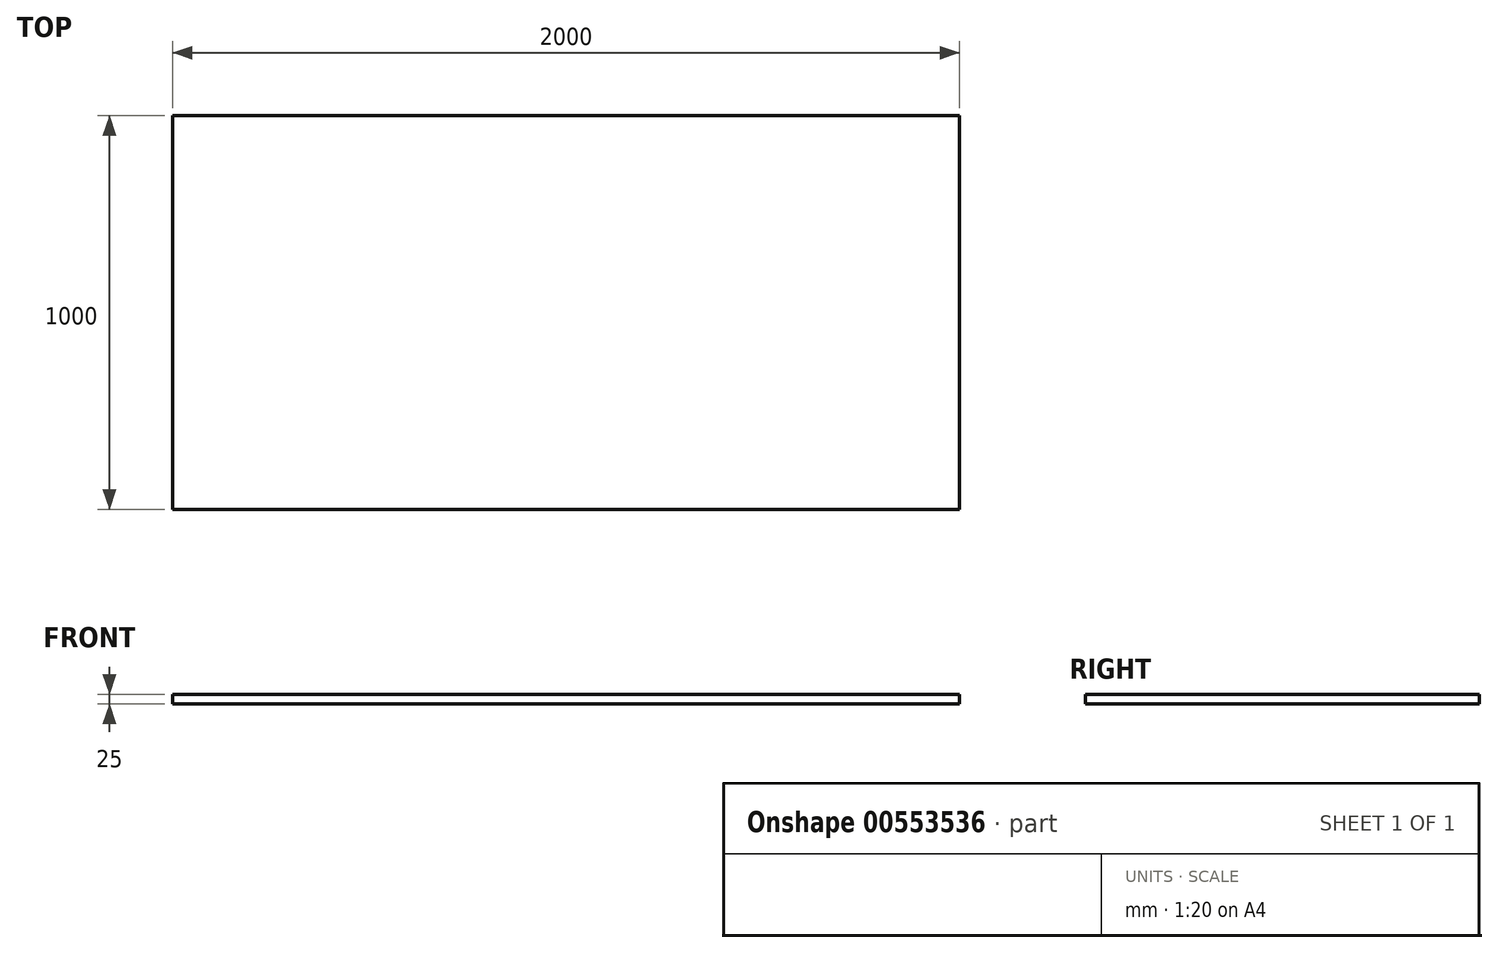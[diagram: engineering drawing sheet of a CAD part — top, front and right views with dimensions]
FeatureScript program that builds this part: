
annotation { "Feature Type Name" : "Feature", "Feature Type Description" : "" }
export const myFeature = defineFeature(function(context is Context, id is Id, definition is map)
    precondition{}
    {
        {
            var Q0;
            Q0=qCreatedBy(makeId("Top.planeOp"),FACE);
            var sketch = newSketch(context, id + "F0", { "sketchPlane" : qUnion([Q0])});
            skLineSegment(sketch, "E0.bottom", {"start": v(-1006.77, 581.78) * mm, "end": v(993.23, 581.78) * mm});
            skLineSegment(sketch, "E0.top", {"start": v(-1006.77, -418.22) * mm, "end": v(993.23, -418.22) * mm});
            skLineSegment(sketch, "E0.left", {"start": v(-1006.77, 581.78) * mm, "end": v(-1006.77, -418.22) * mm});
            skLineSegment(sketch, "E0.right", {"start": v(993.23, 581.78) * mm, "end": v(993.23, -418.22) * mm});
            skLineSegment(sketch, "E1.bottom", {"start": v(-956.77, 531.78) * mm, "end": v(-856.77, 531.78) * mm});
            skLineSegment(sketch, "E1.top", {"start": v(-956.77, 431.78) * mm, "end": v(-856.77, 431.78) * mm});
            skLineSegment(sketch, "E1.left", {"start": v(-956.77, 531.78) * mm, "end": v(-956.77, 431.78) * mm});
            skLineSegment(sketch, "E1.right", {"start": v(-856.77, 531.78) * mm, "end": v(-856.77, 431.78) * mm});
            skLineSegment(sketch, "E2.bottom", {"start": v(-956.77, -268.22) * mm, "end": v(-856.77, -268.22) * mm});
            skLineSegment(sketch, "E2.top", {"start": v(-956.77, -368.22) * mm, "end": v(-856.77, -368.22) * mm});
            skLineSegment(sketch, "E2.left", {"start": v(-956.77, -268.22) * mm, "end": v(-956.77, -368.22) * mm});
            skLineSegment(sketch, "E2.right", {"start": v(-856.77, -268.22) * mm, "end": v(-856.77, -368.22) * mm});
            skLineSegment(sketch, "E3.bottom", {"start": v(843.23, 531.78) * mm, "end": v(943.23, 531.78) * mm});
            skLineSegment(sketch, "E3.top", {"start": v(843.23, 431.78) * mm, "end": v(943.23, 431.78) * mm});
            skLineSegment(sketch, "E3.left", {"start": v(843.23, 531.78) * mm, "end": v(843.23, 431.78) * mm});
            skLineSegment(sketch, "E3.right", {"start": v(943.23, 531.78) * mm, "end": v(943.23, 431.78) * mm});
            skLineSegment(sketch, "E4.bottom", {"start": v(843.23, -268.22) * mm, "end": v(943.23, -268.22) * mm});
            skLineSegment(sketch, "E4.top", {"start": v(843.23, -368.22) * mm, "end": v(943.23, -368.22) * mm});
            skLineSegment(sketch, "E4.left", {"start": v(843.23, -268.22) * mm, "end": v(843.23, -368.22) * mm});
            skLineSegment(sketch, "E4.right", {"start": v(943.23, -268.22) * mm, "end": v(943.23, -368.22) * mm});
            skSolve(sketch);
        }
        {
            var Q0;
            Q0=makeQuery(id+"F0.imprint","IMPRINT",FACE,{"disambiguationData":[TD([[makeQuery(id+"F0.imprint","IMPRINT",EDGE,{"derivedFrom":sQuery(id+"F0.wireOp",EDGE,"E1.bottom")}),-1.0]])]});
            var Q1;
            Q1=makeQuery(id+"F0.imprint","IMPRINT",FACE,{"disambiguationData":[TD([[makeQuery(id+"F0.imprint","IMPRINT",EDGE,{"derivedFrom":sQuery(id+"F0.wireOp",EDGE,"E3.bottom")}),-1.0]])]});
            var Q2;
            Q2=makeQuery(id+"F0.imprint","IMPRINT",FACE,{"disambiguationData":[TD([[makeQuery(id+"F0.imprint","IMPRINT",EDGE,{"derivedFrom":sQuery(id+"F0.wireOp",EDGE,"E4.bottom")}),-1.0]])]});
            var Q3;
            Q3=makeQuery(id+"F0.imprint","IMPRINT",FACE,{"disambiguationData":[TD([[makeQuery(id+"F0.imprint","IMPRINT",EDGE,{"derivedFrom":sQuery(id+"F0.wireOp",EDGE,"E2.bottom")}),-1.0]])]});
            var Q4;
            Q4=makeQuery(id+"F0.imprint","IMPRINT",FACE,{"disambiguationData":[TD([[makeQuery(id+"F0.imprint","IMPRINT",EDGE,{"derivedFrom":sQuery(id+"F0.wireOp",EDGE,"E0.bottom")}),-1.0]])]});
            extrude(context, id + "F1", {"entities" : qUnion([Q0, Q1, Q2, Q3, Q4]), "depth" : 25 * mm, "offsetDistance" : 25 * mm});
        }
    });
